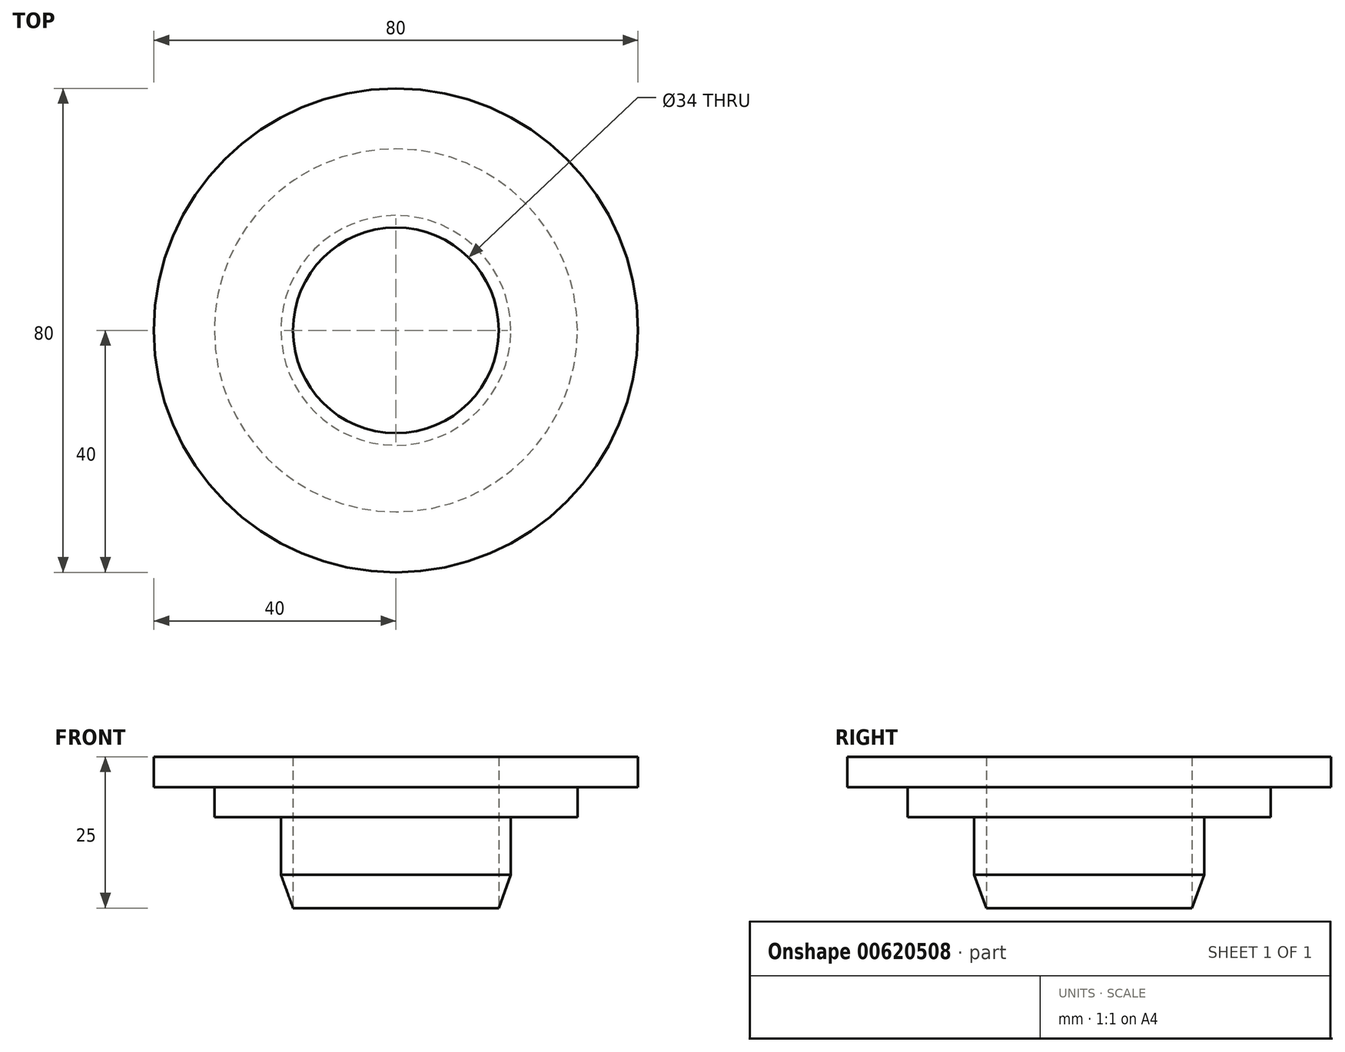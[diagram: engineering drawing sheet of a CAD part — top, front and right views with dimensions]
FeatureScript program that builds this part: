
annotation { "Feature Type Name" : "Feature", "Feature Type Description" : "" }
export const myFeature = defineFeature(function(context is Context, id is Id, definition is map)
    precondition{}
    {
        {
            var Q0;
            Q0=qCreatedBy(makeId("Front.planeOp"),FACE);
            var sketch = newSketch(context, id + "F0", { "sketchPlane" : qUnion([Q0])});
            skLineSegment(sketch, "E0", {"start": v(-17, 0) * mm, "end": v(-17, 25) * mm});
            skLineSegment(sketch, "E1", {"start": v(-17, 25) * mm, "end": v(-40, 25) * mm});
            skLineSegment(sketch, "E2", {"start": v(-40, 25) * mm, "end": v(-40, 20) * mm});
            skLineSegment(sketch, "E3", {"start": v(-19, 5.5) * mm, "end": v(-17, 0) * mm});
            skLineSegment(sketch, "E4", {"start": v(-40, 20) * mm, "end": v(-30, 20) * mm});
            skLineSegment(sketch, "E5", {"start": v(-30, 20) * mm, "end": v(-30, 15) * mm});
            skLineSegment(sketch, "E6", {"start": v(-30, 15) * mm, "end": v(-19, 15) * mm});
            skLineSegment(sketch, "E7", {"start": v(-19, 15) * mm, "end": v(-19, 5.5) * mm});
            skLineSegment(sketch, "E8", {"start": v(0, 0) * mm, "end": v(0, 47.42) * mm, "construction": true});
            skSolve(sketch);
        }
        {
            var Q0;
            Q0=makeQuery(id+"F0.imprint","IMPRINT",FACE,{"disambiguationData":[TD([[makeQuery(id+"F0.imprint","IMPRINT",EDGE,{"derivedFrom":sQuery(id+"F0.wireOp",EDGE,"E0")}),1.0]])]});
            var Q1;
            Q1=sQuery(id+"F0.wireOp",EDGE,"E8");
            revolve(context, id + "F1", {"entities" : qUnion([Q0]), "axis" : qUnion([Q1]), "revolveType" : RevolveType.FULL});
        }
    });
